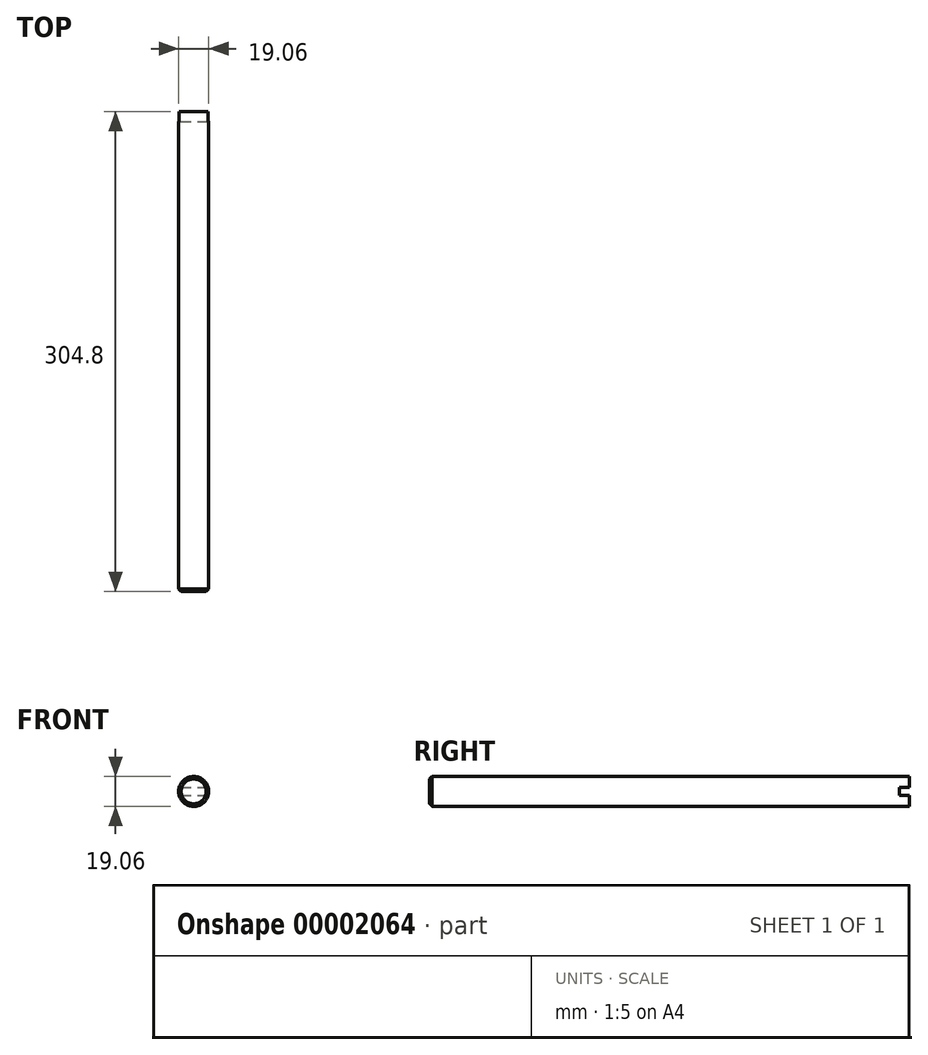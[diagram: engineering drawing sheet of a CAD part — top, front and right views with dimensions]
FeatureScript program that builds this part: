
annotation { "Feature Type Name" : "Feature", "Feature Type Description" : "" }
export const myFeature = defineFeature(function(context is Context, id is Id, definition is map)
    precondition{}
    {
        {
            var Q0;
            Q0=qCreatedBy(makeId("Front.planeOp"),FACE);
            var sketch = newSketch(context, id + "F0", { "sketchPlane" : qUnion([Q0])});
            skCircle(sketch, "E0", {"center": v(0, 0) * mm, "radius": 9.53 * mm});
            skSolve(sketch);
        }
        {
            var Q0;
            Q0=makeQuery(id+"F0.imprint","IMPRINT",FACE,{"disambiguationData":[TD([[makeQuery(id+"F0.imprint","IMPRINT",EDGE,{"derivedFrom":sQuery(id+"F0.wireOp",EDGE,"E0")}),1.0]])]});
            extrude(context, id + "F1", {"entities" : qUnion([Q0]), "depth" : 304.8 * mm});
        }
        {
            var Q0;
            Q0=makeQuery(id+"F1.opExtrude","CAP_FACE",FACE,{"disambiguationData":[OSD([sQuery(id+"F0.wireOp",EDGE,"E0")])],"isStart":true});
            var sketch = newSketch(context, id + "F2", { "sketchPlane" : qUnion([Q0])});
            skLineSegment(sketch, "E1", {"start": v(11.1, 2.54) * mm, "end": v(11.1, -2.54) * mm});
            skLineSegment(sketch, "E2", {"start": v(-11.57, 2.54) * mm, "end": v(-11.57, -2.54) * mm});
            skLineSegment(sketch, "E3", {"start": v(11.1, 2.54) * mm, "end": v(-11.57, 2.54) * mm});
            skLineSegment(sketch, "E4", {"start": v(11.1, -2.54) * mm, "end": v(-11.57, -2.54) * mm});
            skSolve(sketch);
        }
        {
            var Q0;
            {var subQ0=makeQuery(id+"F1.opExtrude","CAP_EDGE",EDGE,{"disambiguationData":[OSD([sQuery(id+"F0.wireOp",EDGE,"E0")])],"isStart":true});var subQ3=sQuery(id+"F2.wireOp",EDGE,"E3");var subQ6=makeQuery(id+"F2.imprint","INTERSECT",VERTEX,{"disambiguationData":[OD(0.0)],"derivedFrom":[subQ0,subQ3]});Q0=makeQuery(id+"F2.imprint","IMPRINT",FACE,{"disambiguationData":[TD([[makeQuery(id+"F2.imprint","IMPRINT",EDGE,{"disambiguationData":[TD([[subQ6,-1.0]])],"derivedFrom":subQ3}),1.0]])]});}
            extrude(context, id + "F3", {"entities" : qUnion([Q0]), "operationType" : NewBodyOperationType.REMOVE, "oppositeDirection" : true, "depth" : 6.35 * mm});
        }
        {
            var Q0;
            Q0=makeQuery(id+"F1.opExtrude","CAP_EDGE",EDGE,{"disambiguationData":[OSD([sQuery(id+"F0.wireOp",EDGE,"E0")])],"isStart":false});
            chamfer(context, id + "F4", {"entities" : qUnion([Q0]), "width" : 1.59 * mm, "tangentPropagation" : true});
        }
    });
